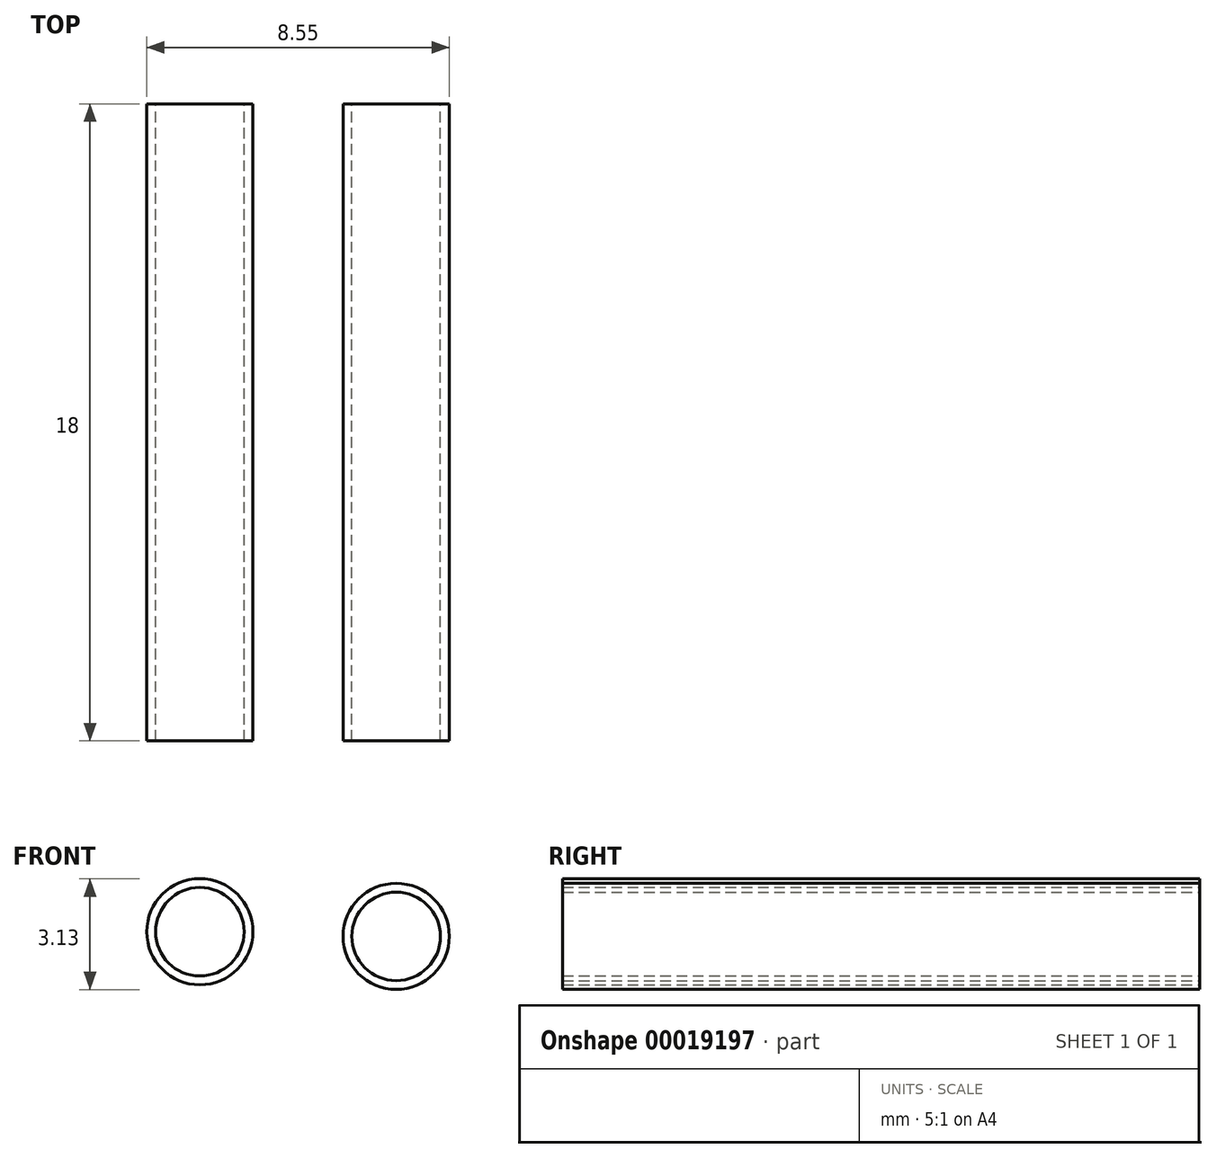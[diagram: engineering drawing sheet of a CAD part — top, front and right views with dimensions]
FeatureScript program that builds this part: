
annotation { "Feature Type Name" : "Feature", "Feature Type Description" : "" }
export const myFeature = defineFeature(function(context is Context, id is Id, definition is map)
    precondition{}
    {
        {
            var Q0;
            Q0=qCreatedBy(makeId("Front.planeOp"),FACE);
            var sketch = newSketch(context, id + "F0", { "sketchPlane" : qUnion([Q0])});
            skCircle(sketch, "E0", {"center": v(-33.94, 12.1) * mm, "radius": 1.5 * mm});
            skCircle(sketch, "E1", {"center": v(-28.4, 11.96) * mm, "radius": 1.5 * mm});
            skCircle(sketch, "E2", {"center": v(-33.94, 12.1) * mm, "radius": 1.25 * mm});
            skCircle(sketch, "E3", {"center": v(-28.4, 11.96) * mm, "radius": 1.25 * mm});
            skSolve(sketch);
        }
        {
            var Q0;
            Q0 = qSketchRegion(id + "F0", true);
            extrude(context, id + "F1", {"entities" : qUnion([Q0]), "depth" : 18 * mm});
        }
    });
